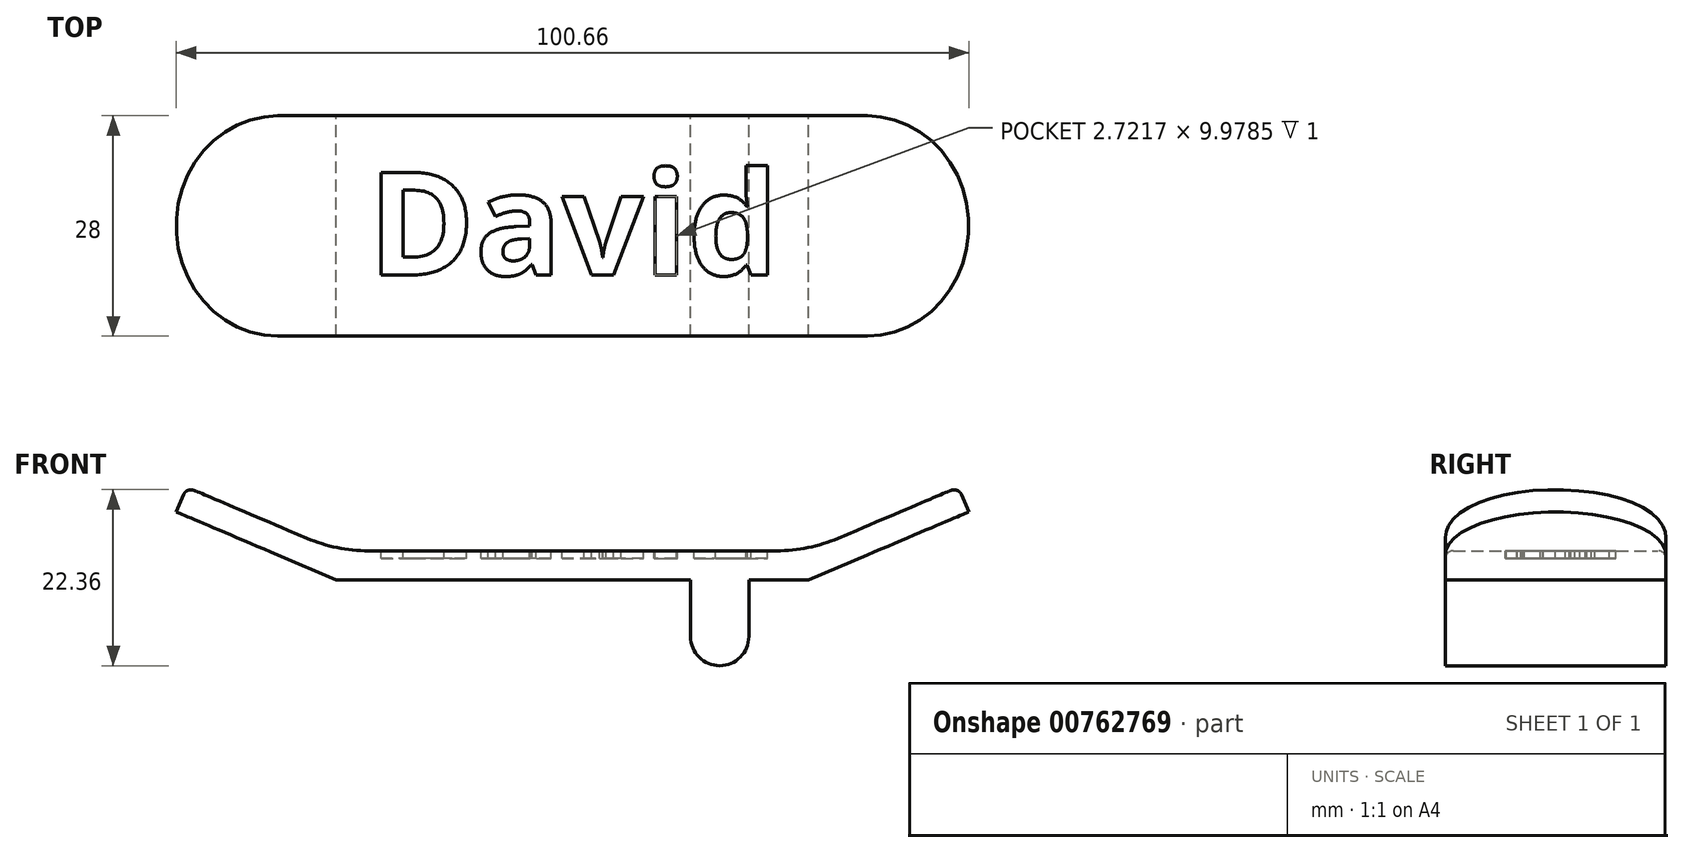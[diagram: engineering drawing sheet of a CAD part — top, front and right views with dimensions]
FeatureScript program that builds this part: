
annotation { "Feature Type Name" : "Feature", "Feature Type Description" : "" }
export const myFeature = defineFeature(function(context is Context, id is Id, definition is map)
    precondition{}
    {
        {
            var Q0;
            Q0=qCreatedBy(makeId("Front.planeOp"),FACE);
            var sketch = newSketch(context, id + "F0", { "sketchPlane" : qUnion([Q0])});
            skLineSegment(sketch, "E0", {"start": v(0, -51.02) * mm, "end": v(0, 51.02) * mm, "construction": true});
            skLineSegment(sketch, "E1", {"start": v(0, 0) * mm, "end": v(30, 0) * mm});
            skLineSegment(sketch, "E2", {"start": v(30, 0) * mm, "end": v(50.33, 8.63) * mm});
            skLineSegment(sketch, "E3", {"start": v(50.33, 8.63) * mm, "end": v(49, 11.76) * mm});
            skLineSegment(sketch, "E4", {"start": v(49, 11.76) * mm, "end": v(30, 3.7) * mm});
            skLineSegment(sketch, "E5", {"start": v(30, 3.7) * mm, "end": v(0, 3.7) * mm});
            skLineSegment(sketch, "E6", {"start": v(15, 0) * mm, "end": v(15, -7.2) * mm});
            skLineSegment(sketch, "E7", {"start": v(22.4, 0) * mm, "end": v(22.4, -7.2) * mm});
            skArc(sketch, "E8", {"start": v(15, -7.2) * mm, "mid": v(18.7, -10.9) * mm, "end": v(22.4, -7.2) * mm});
            skLineSegment(sketch, "E9.MirrorCS", {"start": v(-50.33, 8.63) * mm, "end": v(-49, 11.76) * mm});
            skLineSegment(sketch, "E10.MirrorCS", {"start": v(-30, 0) * mm, "end": v(-50.33, 8.63) * mm});
            skLineSegment(sketch, "E11.MirrorCS", {"start": v(-49, 11.76) * mm, "end": v(-30, 3.7) * mm});
            skLineSegment(sketch, "E12.MirrorCS", {"start": v(0, 0) * mm, "end": v(-30, 0) * mm});
            skLineSegment(sketch, "E13.MirrorCS", {"start": v(-30, 3.7) * mm, "end": v(0, 3.7) * mm});
            skArc(sketch, "E14.MirrorCS", {"start": v(-15, -7.2) * mm, "mid": v(-18.7, -10.9) * mm, "end": v(-22.4, -7.2) * mm});
            skLineSegment(sketch, "E15.MirrorCS", {"start": v(-15, 0) * mm, "end": v(-15, -7.2) * mm});
            skLineSegment(sketch, "E16.MirrorCS", {"start": v(-22.4, 0) * mm, "end": v(-22.4, -7.2) * mm});
            skSolve(sketch);
        }
        {
            var Q0;
            {var subQ6=sQuery(id+"F0.wireOp",EDGE,"E2");Q0=makeQuery(id+"F0.imprint","IMPRINT",FACE,{"disambiguationData":[TD([[makeQuery(id+"F0.imprint","IMPRINT",EDGE,{"derivedFrom":subQ6}),1.0]])]});}
            var Q1;
            Q1=makeQuery(id+"F0.imprint","IMPRINT",FACE,{"disambiguationData":[TD([[makeQuery(id+"F0.imprint","IMPRINT",EDGE,{"derivedFrom":sQuery(id+"F0.wireOp",EDGE,"E14.MirrorCS")}),-1.0]])]});
            var Q2;
            {var subQ2=sQuery(id+"F0.wireOp",EDGE,"E6");Q2=makeQuery(id+"F0.imprint","IMPRINT",FACE,{"disambiguationData":[TD([[makeQuery(id+"F0.imprint","IMPRINT",EDGE,{"derivedFrom":subQ2}),1.0]])]});}
            extrude(context, id + "F1", {"entities" : qUnion([Q0, Q1, Q2]), "depth" : 28 * mm, "offsetDistance" : 25 * mm});
        }
        {
            var Q0;
            Q0=makeQuery(id+"F1.opExtrude","CAP_EDGE",EDGE,{"disambiguationData":[OSD([sQuery(id+"F0.wireOp",EDGE,"E3")])],"isStart":true});
            var Q1;
            Q1=makeQuery(id+"F1.opExtrude","CAP_EDGE",EDGE,{"disambiguationData":[OSD([sQuery(id+"F0.wireOp",EDGE,"E3")])],"isStart":false});
            var Q2;
            Q2=makeQuery(id+"F1.opExtrude","CAP_EDGE",EDGE,{"disambiguationData":[OSD([sQuery(id+"F0.wireOp",EDGE,"E9.MirrorCS")])],"isStart":true});
            var Q3;
            Q3=makeQuery(id+"F1.opExtrude","CAP_EDGE",EDGE,{"disambiguationData":[OSD([sQuery(id+"F0.wireOp",EDGE,"E9.MirrorCS")])],"isStart":false});
            fillet(context, id + "F2", {"entities" : qUnion([Q0, Q1, Q2, Q3]), "tangentPropagation" : true, "radius" : 14 * mm, "defaultsChanged" : true, "vertexSettings" : [], "allowEdgeOverflow" : false});
        }
        {
            var Q0;
            Q0=makeQuery(id+"F1.opExtrude","SWEPT_EDGE",EDGE,{"disambiguationData":[OSD([sQuery(id+"F0.wireOp",EDGE,"E4"),sQuery(id+"F0.wireOp",EDGE,"E5")])]});
            var Q1;
            Q1=makeQuery(id+"F1.opExtrude","SWEPT_EDGE",EDGE,{"disambiguationData":[OSD([sQuery(id+"F0.wireOp",EDGE,"E11.MirrorCS"),sQuery(id+"F0.wireOp",EDGE,"E13.MirrorCS")])]});
            fillet(context, id + "F3", {"entities" : qUnion([Q0, Q1]), "tangentPropagation" : true, "radius" : 20 * mm, "defaultsChanged" : true, "vertexSettings" : [], "allowEdgeOverflow" : false});
        }
        {
            var Q0;
            Q0=makeQuery(id+"F1.opExtrude","SWEPT_FACE",FACE,{"disambiguationData":[OSD([sQuery(id+"F0.wireOp",EDGE,"E5"),sQuery(id+"F0.wireOp",EDGE,"E13.MirrorCS")])]});
            fillet(context, id + "F4", {"entities" : qUnion([Q0]), "tangentPropagation" : true, "radius" : 1 * mm, "defaultsChanged" : false, "vertexSettings" : [], "allowEdgeOverflow" : false});
        }
        {
            var Q0;
            Q0=makeQuery(id+"F1.opExtrude","SWEPT_FACE",FACE,{"disambiguationData":[OSD([sQuery(id+"F0.wireOp",EDGE,"E5"),sQuery(id+"F0.wireOp",EDGE,"E13.MirrorCS")])]});
            var sketch = newSketch(context, id + "F5", { "sketchPlane" : qUnion([Q0])});
            skText(sketch, "E17", { "text": "David", "fontName": "OpenSans-Bold.ttf"});
            const initialGuessF5  = {"E17": [-0.02593, -0.02024, 1, 0, 0.01316]};
            skSetInitialGuess(sketch, initialGuessF5);
            skSolve(sketch);
        }
        {
            var Q0;
            Q0 = qSketchRegion(id + "F5", true);
            extrude(context, id + "F6", {"entities" : qUnion([Q0]), "operationType" : NewBodyOperationType.REMOVE, "oppositeDirection" : true, "depth" : 1 * mm, "offsetDistance" : 25 * mm});
        }
    });
